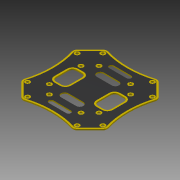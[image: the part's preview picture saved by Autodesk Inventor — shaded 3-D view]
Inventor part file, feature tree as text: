
AUTODESK INVENTOR PART (.ipt)
format: ipt  version: 2015 (Build 190159000, 159)  size: 508,928 bytes
history: native  units: in
note: dims shown in document units (in); Inventor stores cm internally (conversion verified against a paired STEP export)
features: mirror x1, other x1, imported_body x1
ambient origin geometry x8: Origin, YZ Plane, XZ Plane, XY Plane, X Axis, Y Axis, Z Axis, Center Point
bodies: Body1 (feature_tree)
feature tree (3):
  mirror  "Mirror1"
  other  "F450 Top Plate1"
  imported_body  "Base1"
